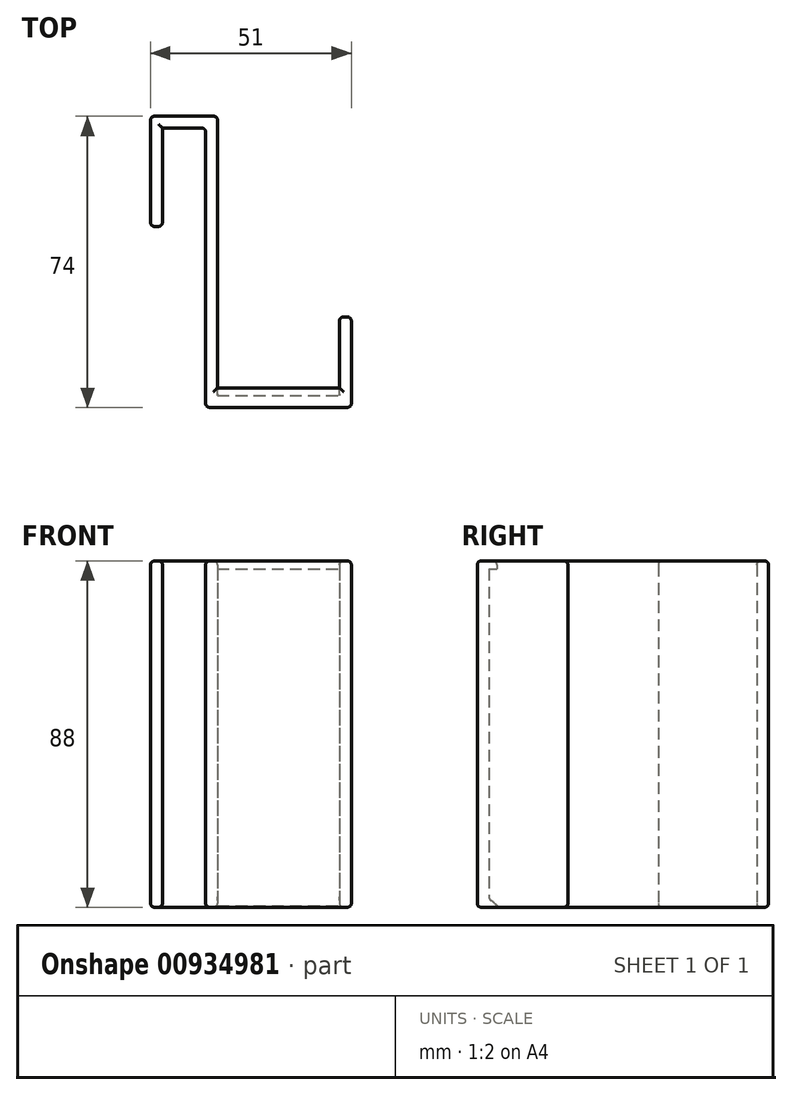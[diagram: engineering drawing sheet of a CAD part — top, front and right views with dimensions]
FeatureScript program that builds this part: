
annotation { "Feature Type Name" : "Feature", "Feature Type Description" : "" }
export const myFeature = defineFeature(function(context is Context, id is Id, definition is map)
    precondition{}
    {
        {
            var Q0;
            Q0=qCreatedBy(makeId("Top.planeOp"),FACE);
            var sketch = newSketch(context, id + "F0", { "sketchPlane" : qUnion([Q0])});
            skLineSegment(sketch, "E0.bottom", {"start": v(0, 0) * mm, "end": v(3, 0) * mm});
            skLineSegment(sketch, "E0.top", {"start": v(0, 68) * mm, "end": v(3, 68) * mm});
            skLineSegment(sketch, "E0.left", {"start": v(0, 0) * mm, "end": v(0, 68) * mm});
            skLineSegment(sketch, "E0.right", {"start": v(3, 0) * mm, "end": v(3, 68) * mm});
            skLineSegment(sketch, "E1.bottom", {"start": v(3, 68) * mm, "end": v(-11, 68) * mm});
            skLineSegment(sketch, "E1.top", {"start": v(3, 71) * mm, "end": v(-11, 71) * mm});
            skLineSegment(sketch, "E1.left", {"start": v(3, 68) * mm, "end": v(3, 71) * mm});
            skLineSegment(sketch, "E1.right", {"start": v(-11, 68) * mm, "end": v(-11, 71) * mm});
            skLineSegment(sketch, "E2.bottom", {"start": v(-11, 71) * mm, "end": v(-14, 71) * mm});
            skLineSegment(sketch, "E2.top", {"start": v(-11, 43) * mm, "end": v(-14, 43) * mm});
            skLineSegment(sketch, "E2.left", {"start": v(-11, 71) * mm, "end": v(-11, 43) * mm});
            skLineSegment(sketch, "E2.right", {"start": v(-14, 71) * mm, "end": v(-14, 43) * mm});
            skLineSegment(sketch, "E3.bottom", {"start": v(0, 0) * mm, "end": v(34, 0) * mm});
            skLineSegment(sketch, "E3.top", {"start": v(0, -3) * mm, "end": v(34, -3) * mm});
            skLineSegment(sketch, "E3.left", {"start": v(0, 0) * mm, "end": v(0, -3) * mm});
            skLineSegment(sketch, "E3.right", {"start": v(34, 0) * mm, "end": v(34, -3) * mm});
            skLineSegment(sketch, "E4.bottom", {"start": v(34, -3) * mm, "end": v(37, -3) * mm});
            skLineSegment(sketch, "E4.top", {"start": v(34, 20) * mm, "end": v(37, 20) * mm});
            skLineSegment(sketch, "E4.left", {"start": v(34, -3) * mm, "end": v(34, 20) * mm});
            skLineSegment(sketch, "E4.right", {"start": v(37, -3) * mm, "end": v(37, 20) * mm});
            skLineSegment(sketch, "E5.bottom", {"start": v(3, 0) * mm, "end": v(34, 0) * mm});
            skLineSegment(sketch, "E5.top", {"start": v(3, 2) * mm, "end": v(34, 2) * mm});
            skLineSegment(sketch, "E5.left", {"start": v(3, 0) * mm, "end": v(3, 2) * mm});
            skLineSegment(sketch, "E5.right", {"start": v(34, 0) * mm, "end": v(34, 2) * mm});
            skSolve(sketch);
        }
        {
            var Q0;
            Q0=makeQuery(id+"F0.imprint","IMPRINT",FACE,{"disambiguationData":[TD([[makeQuery(id+"F0.imprint","IMPRINT",EDGE,{"derivedFrom":sQuery(id+"F0.wireOp",EDGE,"E1.right")}),1.0]])]});
            var Q1;
            Q1=makeQuery(id+"F0.imprint","IMPRINT",FACE,{"disambiguationData":[TD([[makeQuery(id+"F0.imprint","IMPRINT",EDGE,{"derivedFrom":sQuery(id+"F0.wireOp",EDGE,"E0.top")}),1.0]])]});
            var Q2;
            {var subQ3=sQuery(id+"F0.wireOp",EDGE,"E3.right");Q2=makeQuery(id+"F0.imprint","IMPRINT",FACE,{"disambiguationData":[TD([[makeQuery(id+"F0.imprint","IMPRINT",EDGE,{"derivedFrom":subQ3}),1.0]])]});}
            var Q3;
            {var subQ3=sQuery(id+"F0.wireOp",EDGE,"E0.bottom");Q3=makeQuery(id+"F0.imprint","IMPRINT",FACE,{"disambiguationData":[TD([[makeQuery(id+"F0.imprint","IMPRINT",EDGE,{"derivedFrom":subQ3}),1.0]])]});}
            var Q4;
            Q4=makeQuery(id+"F0.imprint","IMPRINT",FACE,{"disambiguationData":[TD([[makeQuery(id+"F0.imprint","IMPRINT",EDGE,{"derivedFrom":sQuery(id+"F0.wireOp",EDGE,"E0.bottom")}),-1.0]])]});
            extrude(context, id + "F1", {"entities" : qUnion([Q0, Q1, Q2, Q3, Q4]), "endBound" : BoundingType.SYMMETRIC, "depth" : 88 * mm, "offsetDistance" : 25 * mm});
        }
        {
            var Q0;
            {var subQ0=sQuery(id+"F0.wireOp",EDGE,"E3.bottom");Q0=makeQuery(id+"F0.imprint","IMPRINT",FACE,{"disambiguationData":[TD([[makeQuery(id+"F0.imprint","IMPRINT",EDGE,{"derivedFrom":subQ0}),1.0]])]});}
            extrude(context, id + "F2", {"entities" : qUnion([Q0]), "operationType" : NewBodyOperationType.ADD, "endBound" : BoundingType.SYMMETRIC, "depth" : 88 * mm, "offsetDistance" : 25 * mm});
        }
        {
            var Q0;
            {var subQ0=sQuery(id+"F0.wireOp",EDGE,"E3.bottom");Q0=makeQuery(id+"F0.imprint","IMPRINT",FACE,{"disambiguationData":[TD([[makeQuery(id+"F0.imprint","IMPRINT",EDGE,{"derivedFrom":subQ0}),1.0]])]});}
            extrude(context, id + "F3", {"entities" : qUnion([Q0]), "operationType" : NewBodyOperationType.REMOVE, "endBound" : BoundingType.SYMMETRIC, "depth" : 84 * mm, "offsetDistance" : 25 * mm});
        }
        {
            var Q0;
            Q0=makeQuery(id+"F3.boolean.opBoolean","COPY",EDGE,{"derivedFrom":makeQuery(id+"F3.opExtrude","CAP_EDGE",EDGE,{"disambiguationData":[OSD([sQuery(id+"F0.wireOp",EDGE,"E5.top")])],"isStart":true})});
            var Q1;
            Q1=makeQuery(id+"F3.boolean.opBoolean","COPY",EDGE,{"derivedFrom":makeQuery(id+"F3.opExtrude","CAP_EDGE",EDGE,{"disambiguationData":[OSD([sQuery(id+"F0.wireOp",EDGE,"E5.top")])],"isStart":false})});
            chamfer(context, id + "F4", {"entities" : qUnion([Q0, Q1]), "width" : 1.6 * mm, "tangentPropagation" : true});
        }
        {
            var Q0;
            {var subQ0=sQuery(id+"F0.wireOp",EDGE,"E5.top");Q0=makeQuery(id+"F4.opChamfer","BLEND_EDGE",EDGE,{"blendedFrom":[makeQuery(id+"F3.boolean.opBoolean","COPY",EDGE,{"derivedFrom":makeQuery(id+"F3.opExtrude","CAP_EDGE",EDGE,{"disambiguationData":[OSD([subQ0])],"isStart":false})}),makeQuery(id+"F3.boolean.opBoolean","COPY",FACE,{"derivedFrom":makeQuery(id+"F3.opExtrude","CAP_FACE",FACE,{"disambiguationData":[OSD([sQuery(id+"F0.wireOp",EDGE,"E0.right"),sQuery(id+"F0.wireOp",EDGE,"E3.bottom"),sQuery(id+"F0.wireOp",EDGE,"E4.left"),subQ0])],"isStart":false})})],"blendedInto":[makeQuery(id+"F3.boolean.opBoolean","COPY",FACE,{"derivedFrom":makeQuery(id+"F3.opExtrude","CAP_FACE",FACE,{"disambiguationData":[OSD([sQuery(id+"F0.wireOp",EDGE,"E0.right"),sQuery(id+"F0.wireOp",EDGE,"E3.bottom"),sQuery(id+"F0.wireOp",EDGE,"E4.left"),subQ0])],"isStart":false})})]});}
            var Q1;
            {var subQ0=sQuery(id+"F0.wireOp",EDGE,"E5.top");Q1=makeQuery(id+"F4.opChamfer","BLEND_EDGE",EDGE,{"blendedFrom":[makeQuery(id+"F3.boolean.opBoolean","COPY",EDGE,{"derivedFrom":makeQuery(id+"F3.opExtrude","CAP_EDGE",EDGE,{"disambiguationData":[OSD([subQ0])],"isStart":true})}),makeQuery(id+"F3.boolean.opBoolean","COPY",FACE,{"derivedFrom":makeQuery(id+"F3.opExtrude","CAP_FACE",FACE,{"disambiguationData":[OSD([sQuery(id+"F0.wireOp",EDGE,"E0.right"),sQuery(id+"F0.wireOp",EDGE,"E3.bottom"),sQuery(id+"F0.wireOp",EDGE,"E4.left"),subQ0])],"isStart":true})})],"blendedInto":[makeQuery(id+"F3.boolean.opBoolean","COPY",FACE,{"derivedFrom":makeQuery(id+"F3.opExtrude","CAP_FACE",FACE,{"disambiguationData":[OSD([sQuery(id+"F0.wireOp",EDGE,"E0.right"),sQuery(id+"F0.wireOp",EDGE,"E3.bottom"),sQuery(id+"F0.wireOp",EDGE,"E4.left"),subQ0])],"isStart":true})})]});}
            fillet(context, id + "F5", {"entities" : qUnion([Q0, Q1]), "radius" : 5 * mm, "tangentPropagation" : true, "allowEdgeOverflow" : false});
        }
        {
            var Q0;
            {var subQ0=sQuery(id+"F0.wireOp",EDGE,"E3.bottom");var subQ1=sQuery(id+"F0.wireOp",EDGE,"E5.top");Q0=makeQuery(id+"F5.opFillet","BLEND_EDGE",EDGE,{"blendedFrom":[makeQuery(id+"F4.opChamfer","BLEND_EDGE",EDGE,{"blendedFrom":[makeQuery(id+"F3.boolean.opBoolean","COPY",EDGE,{"derivedFrom":makeQuery(id+"F3.opExtrude","CAP_EDGE",EDGE,{"disambiguationData":[OSD([subQ1])],"isStart":true})}),makeQuery(id+"F3.boolean.opBoolean","COPY",FACE,{"derivedFrom":makeQuery(id+"F3.opExtrude","CAP_FACE",FACE,{"disambiguationData":[OSD([sQuery(id+"F0.wireOp",EDGE,"E0.right"),subQ0,sQuery(id+"F0.wireOp",EDGE,"E4.left"),subQ1])],"isStart":true})})],"blendedInto":[makeQuery(id+"F3.boolean.opBoolean","COPY",FACE,{"derivedFrom":makeQuery(id+"F3.opExtrude","CAP_FACE",FACE,{"disambiguationData":[OSD([sQuery(id+"F0.wireOp",EDGE,"E0.right"),subQ0,sQuery(id+"F0.wireOp",EDGE,"E4.left"),subQ1])],"isStart":true})})]}),makeQuery(id+"F3.boolean.opBoolean","COPY",FACE,{"derivedFrom":makeQuery(id+"F3.opExtrude","SWEPT_FACE",FACE,{"disambiguationData":[OSD([subQ0])]})})],"blendedInto":[makeQuery(id+"F3.boolean.opBoolean","COPY",FACE,{"derivedFrom":makeQuery(id+"F3.opExtrude","SWEPT_FACE",FACE,{"disambiguationData":[OSD([subQ0])]})})]});}
            var Q1;
            {var subQ0=sQuery(id+"F0.wireOp",EDGE,"E3.bottom");var subQ1=sQuery(id+"F0.wireOp",EDGE,"E5.top");Q1=makeQuery(id+"F5.opFillet","BLEND_EDGE",EDGE,{"blendedFrom":[makeQuery(id+"F4.opChamfer","BLEND_EDGE",EDGE,{"blendedFrom":[makeQuery(id+"F3.boolean.opBoolean","COPY",EDGE,{"derivedFrom":makeQuery(id+"F3.opExtrude","CAP_EDGE",EDGE,{"disambiguationData":[OSD([subQ1])],"isStart":false})}),makeQuery(id+"F3.boolean.opBoolean","COPY",FACE,{"derivedFrom":makeQuery(id+"F3.opExtrude","CAP_FACE",FACE,{"disambiguationData":[OSD([sQuery(id+"F0.wireOp",EDGE,"E0.right"),subQ0,sQuery(id+"F0.wireOp",EDGE,"E4.left"),subQ1])],"isStart":false})})],"blendedInto":[makeQuery(id+"F3.boolean.opBoolean","COPY",FACE,{"derivedFrom":makeQuery(id+"F3.opExtrude","CAP_FACE",FACE,{"disambiguationData":[OSD([sQuery(id+"F0.wireOp",EDGE,"E0.right"),subQ0,sQuery(id+"F0.wireOp",EDGE,"E4.left"),subQ1])],"isStart":false})})]}),makeQuery(id+"F3.boolean.opBoolean","COPY",FACE,{"derivedFrom":makeQuery(id+"F3.opExtrude","SWEPT_FACE",FACE,{"disambiguationData":[OSD([subQ0])]})})],"blendedInto":[makeQuery(id+"F3.boolean.opBoolean","COPY",FACE,{"derivedFrom":makeQuery(id+"F3.opExtrude","SWEPT_FACE",FACE,{"disambiguationData":[OSD([subQ0])]})})]});}
            fillet(context, id + "F6", {"entities" : qUnion([Q0, Q1]), "radius" : 1 * mm, "tangentPropagation" : true, "allowEdgeOverflow" : false});
        }
        {
            var Q0;
            Q0=makeQuery(id+"F1.opExtrude","SWEPT_EDGE",EDGE,{"disambiguationData":[OSD([sQuery(id+"F0.wireOp",EDGE,"E1.top"),sQuery(id+"F0.wireOp",EDGE,"E1.left")])]});
            var Q1;
            Q1=makeQuery(id+"F1.opExtrude","CAP_EDGE",EDGE,{"disambiguationData":[OSD([sQuery(id+"F0.wireOp",EDGE,"E1.top"),sQuery(id+"F0.wireOp",EDGE,"E2.bottom")])],"isStart":false});
            var Q2;
            Q2=makeQuery(id+"F1.opExtrude","CAP_EDGE",EDGE,{"disambiguationData":[OSD([sQuery(id+"F0.wireOp",EDGE,"E1.top"),sQuery(id+"F0.wireOp",EDGE,"E2.bottom")])],"isStart":true});
            var Q3;
            Q3=makeQuery(id+"F1.opExtrude","SWEPT_EDGE",EDGE,{"disambiguationData":[OSD([sQuery(id+"F0.wireOp",EDGE,"E2.bottom"),sQuery(id+"F0.wireOp",EDGE,"E2.right")])]});
            var Q4;
            Q4=makeQuery(id+"F1.opExtrude","CAP_EDGE",EDGE,{"disambiguationData":[OSD([sQuery(id+"F0.wireOp",EDGE,"E2.right")])],"isStart":true});
            var Q5;
            Q5=makeQuery(id+"F1.opExtrude","SWEPT_EDGE",EDGE,{"disambiguationData":[OSD([sQuery(id+"F0.wireOp",EDGE,"E2.top"),sQuery(id+"F0.wireOp",EDGE,"E2.right")])]});
            var Q6;
            Q6=makeQuery(id+"F1.opExtrude","CAP_EDGE",EDGE,{"disambiguationData":[OSD([sQuery(id+"F0.wireOp",EDGE,"E2.right")])],"isStart":false});
            var Q7;
            Q7=makeQuery(id+"F1.opExtrude","CAP_EDGE",EDGE,{"disambiguationData":[OSD([sQuery(id+"F0.wireOp",EDGE,"E2.left")])],"isStart":true});
            var Q8;
            Q8=makeQuery(id+"F1.opExtrude","CAP_EDGE",EDGE,{"disambiguationData":[OSD([sQuery(id+"F0.wireOp",EDGE,"E1.bottom")])],"isStart":true});
            var Q9;
            Q9=makeQuery(id+"F1.opExtrude","CAP_EDGE",EDGE,{"disambiguationData":[OSD([sQuery(id+"F0.wireOp",EDGE,"E2.top")])],"isStart":true});
            var Q10;
            Q10=makeQuery(id+"F1.opExtrude","SWEPT_EDGE",EDGE,{"disambiguationData":[OSD([sQuery(id+"F0.wireOp",EDGE,"E2.top"),sQuery(id+"F0.wireOp",EDGE,"E2.left")])]});
            var Q11;
            Q11=makeQuery(id+"F1.opExtrude","CAP_EDGE",EDGE,{"disambiguationData":[OSD([sQuery(id+"F0.wireOp",EDGE,"E2.left")])],"isStart":false});
            var Q12;
            Q12=makeQuery(id+"F1.opExtrude","CAP_EDGE",EDGE,{"disambiguationData":[OSD([sQuery(id+"F0.wireOp",EDGE,"E2.top")])],"isStart":false});
            var Q13;
            Q13=makeQuery(id+"F1.opExtrude","CAP_EDGE",EDGE,{"disambiguationData":[OSD([sQuery(id+"F0.wireOp",EDGE,"E1.bottom")])],"isStart":false});
            var Q14;
            Q14=makeQuery(id+"F1.opExtrude","CAP_EDGE",EDGE,{"disambiguationData":[OSD([sQuery(id+"F0.wireOp",EDGE,"E0.left"),sQuery(id+"F0.wireOp",EDGE,"E3.left")])],"isStart":false});
            var Q15;
            Q15=makeQuery(id+"F1.opExtrude","CAP_EDGE",EDGE,{"disambiguationData":[OSD([sQuery(id+"F0.wireOp",EDGE,"E0.right"),sQuery(id+"F0.wireOp",EDGE,"E1.left")])],"isStart":false});
            var Q16;
            Q16=makeQuery(id+"F1.opExtrude","SWEPT_EDGE",EDGE,{"disambiguationData":[OSD([sQuery(id+"F0.wireOp",EDGE,"E0.top"),sQuery(id+"F0.wireOp",EDGE,"E0.left"),sQuery(id+"F0.wireOp",EDGE,"E1.bottom")])]});
            var Q17;
            Q17=makeQuery(id+"F1.opExtrude","SWEPT_EDGE",EDGE,{"disambiguationData":[OSD([sQuery(id+"F0.wireOp",EDGE,"E3.top"),sQuery(id+"F0.wireOp",EDGE,"E3.left")])]});
            var Q18;
            Q18=makeQuery(id+"F1.opExtrude","CAP_EDGE",EDGE,{"disambiguationData":[OSD([sQuery(id+"F0.wireOp",EDGE,"E3.top"),sQuery(id+"F0.wireOp",EDGE,"E4.bottom")])],"isStart":true});
            var Q19;
            Q19=makeQuery(id+"F1.opExtrude","SWEPT_FACE",FACE,{"disambiguationData":[OSD([sQuery(id+"F0.wireOp",EDGE,"E3.top"),sQuery(id+"F0.wireOp",EDGE,"E4.bottom")])]});
            var Q20;
            {var subQ0=sQuery(id+"F0.wireOp",EDGE,"E4.left");var subQ1=sQuery(id+"F0.wireOp",EDGE,"E3.bottom");var subQ2=sQuery(id+"F0.wireOp",EDGE,"E0.right");Q20=makeQuery(id+"F2.boolean.opBoolean","MERGE",FACE,{"derivedFrom":[makeQuery(id+"F1.opExtrude","CAP_FACE",FACE,{"disambiguationData":[OSD([sQuery(id+"F0.wireOp",EDGE,"E0.left"),subQ2,sQuery(id+"F0.wireOp",EDGE,"E1.bottom"),sQuery(id+"F0.wireOp",EDGE,"E1.top"),sQuery(id+"F0.wireOp",EDGE,"E1.left"),sQuery(id+"F0.wireOp",EDGE,"E2.bottom"),sQuery(id+"F0.wireOp",EDGE,"E2.top"),sQuery(id+"F0.wireOp",EDGE,"E2.left"),sQuery(id+"F0.wireOp",EDGE,"E2.right"),subQ1,sQuery(id+"F0.wireOp",EDGE,"E3.top"),sQuery(id+"F0.wireOp",EDGE,"E3.left"),sQuery(id+"F0.wireOp",EDGE,"E4.bottom"),sQuery(id+"F0.wireOp",EDGE,"E4.top"),subQ0,sQuery(id+"F0.wireOp",EDGE,"E4.right")])],"isStart":true}),makeQuery(id+"F2.opExtrude","CAP_FACE",FACE,{"disambiguationData":[OSD([subQ2,subQ1,subQ0,sQuery(id+"F0.wireOp",EDGE,"E5.top")])],"isStart":true})]});}
            var Q21;
            Q21=makeQuery(id+"F1.opExtrude","SWEPT_FACE",FACE,{"disambiguationData":[OSD([sQuery(id+"F0.wireOp",EDGE,"E4.right")])]});
            var Q22;
            Q22=makeQuery(id+"F1.opExtrude","SWEPT_FACE",FACE,{"disambiguationData":[OSD([sQuery(id+"F0.wireOp",EDGE,"E4.top")])]});
            var Q23;
            Q23=makeQuery(id+"F1.opExtrude","CAP_EDGE",EDGE,{"disambiguationData":[OSD([sQuery(id+"F0.wireOp",EDGE,"E4.left")])],"isStart":false});
            var Q24;
            {var subQ0=sQuery(id+"F0.wireOp",EDGE,"E4.left");var subQ1=sQuery(id+"F0.wireOp",EDGE,"E3.bottom");var subQ2=sQuery(id+"F0.wireOp",EDGE,"E0.right");Q24=makeQuery(id+"F2.boolean.opBoolean","MERGE",FACE,{"derivedFrom":[makeQuery(id+"F1.opExtrude","CAP_FACE",FACE,{"disambiguationData":[OSD([sQuery(id+"F0.wireOp",EDGE,"E0.left"),subQ2,sQuery(id+"F0.wireOp",EDGE,"E1.bottom"),sQuery(id+"F0.wireOp",EDGE,"E1.top"),sQuery(id+"F0.wireOp",EDGE,"E1.left"),sQuery(id+"F0.wireOp",EDGE,"E2.bottom"),sQuery(id+"F0.wireOp",EDGE,"E2.top"),sQuery(id+"F0.wireOp",EDGE,"E2.left"),sQuery(id+"F0.wireOp",EDGE,"E2.right"),subQ1,sQuery(id+"F0.wireOp",EDGE,"E3.top"),sQuery(id+"F0.wireOp",EDGE,"E3.left"),sQuery(id+"F0.wireOp",EDGE,"E4.bottom"),sQuery(id+"F0.wireOp",EDGE,"E4.top"),subQ0,sQuery(id+"F0.wireOp",EDGE,"E4.right")])],"isStart":false}),makeQuery(id+"F2.opExtrude","CAP_FACE",FACE,{"disambiguationData":[OSD([subQ2,subQ1,subQ0,sQuery(id+"F0.wireOp",EDGE,"E5.top")])],"isStart":false})]});}
            fillet(context, id + "F7", {"entities" : qUnion([Q0, Q1, Q2, Q3, Q4, Q5, Q6, Q7, Q8, Q9, Q10, Q11, Q12, Q13, Q14, Q15, Q16, Q17, Q18, Q19, Q20, Q21, Q22, Q23, Q24]), "radius" : 1 * mm, "tangentPropagation" : true, "allowEdgeOverflow" : false});
        }
    });
